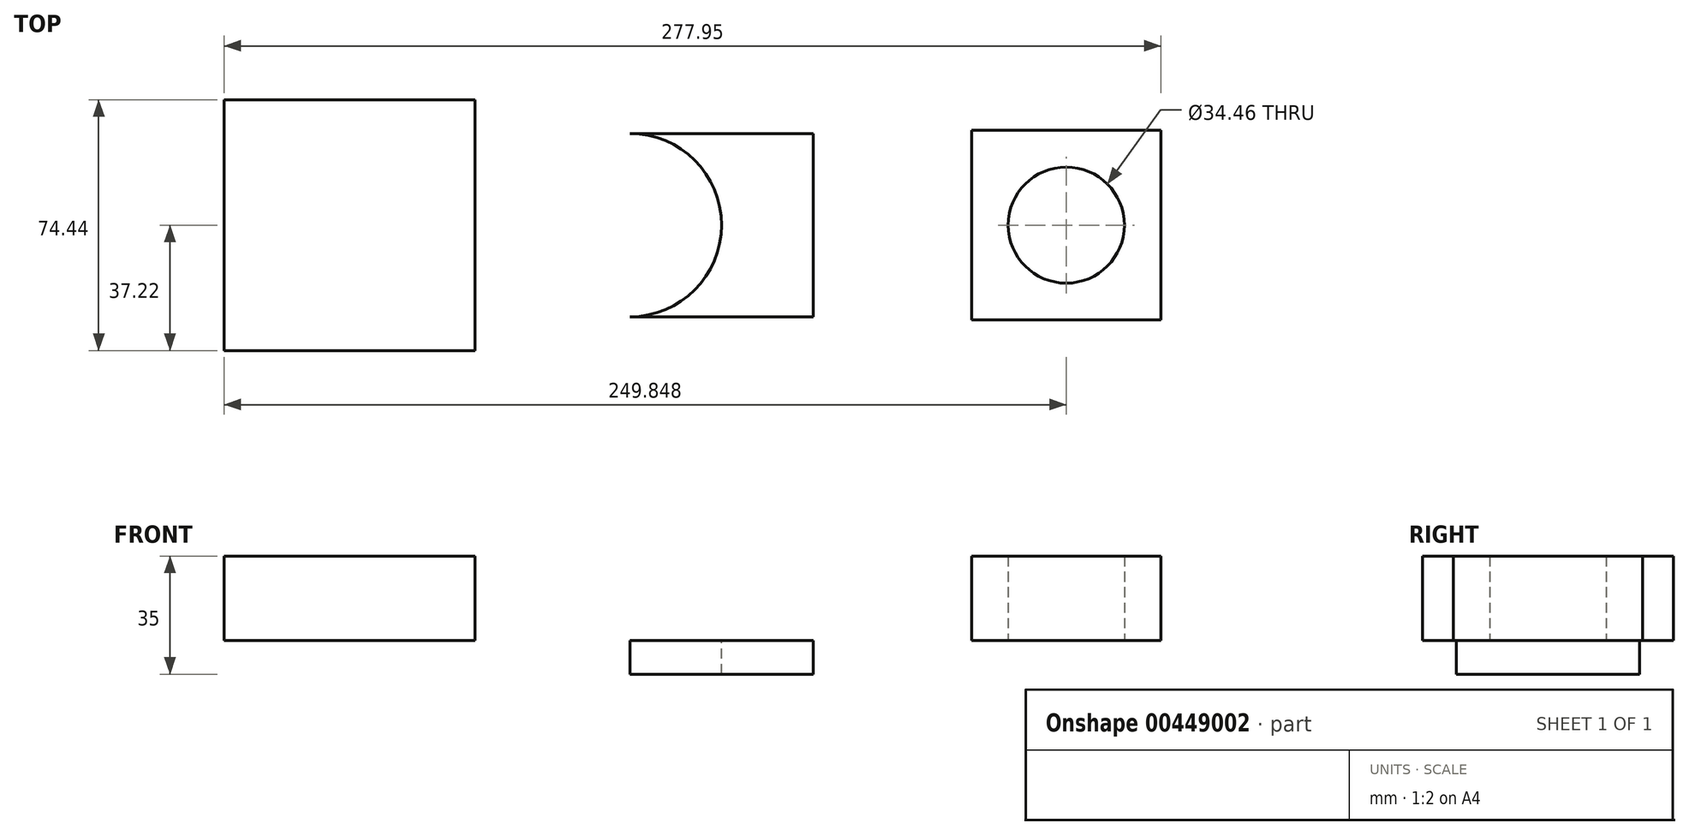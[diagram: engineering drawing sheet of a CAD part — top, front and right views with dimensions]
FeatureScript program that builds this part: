
annotation { "Feature Type Name" : "Feature", "Feature Type Description" : "" }
export const myFeature = defineFeature(function(context is Context, id is Id, definition is map)
    precondition{}
    {
        {
            var Q0;
            Q0=qCreatedBy(makeId("Top.planeOp"),FACE);
            var sketch = newSketch(context, id + "F0", { "sketchPlane" : qUnion([Q0])});
            skLineSegment(sketch, "E0.bottom", {"start": v(-37.22, 37.22) * mm, "end": v(37.22, 37.22) * mm});
            skLineSegment(sketch, "E0.top", {"start": v(-37.22, -37.22) * mm, "end": v(37.22, -37.22) * mm});
            skLineSegment(sketch, "E0.left", {"start": v(-37.22, 37.22) * mm, "end": v(-37.22, -37.22) * mm});
            skLineSegment(sketch, "E0.right", {"start": v(37.22, 37.22) * mm, "end": v(37.22, -37.22) * mm});
            skPoint(sketch, "E0.middle", {"position": v(0, 0) * mm});
            skSolve(sketch);
        }
        {
            var Q0;
            Q0=makeQuery(id+"F0.imprint","IMPRINT",FACE,{"disambiguationData":[TD([[makeQuery(id+"F0.imprint","IMPRINT",EDGE,{"derivedFrom":sQuery(id+"F0.wireOp",EDGE,"E0.bottom")}),-1.0]])]});
            extrude(context, id + "F1", {"entities" : qUnion([Q0]), "depth" : 25 * mm});
        }
        {
            var Q0;
            Q0=qCreatedBy(makeId("Top.planeOp"),FACE);
            var sketch = newSketch(context, id + "F2", { "sketchPlane" : qUnion([Q0])});
            skLineSegment(sketch, "E1.bottom", {"start": v(83.19, 27.19) * mm, "end": v(137.56, 27.19) * mm});
            skLineSegment(sketch, "E1.top", {"start": v(83.19, -27.19) * mm, "end": v(137.56, -27.19) * mm});
            skLineSegment(sketch, "E1.left", {"start": v(83.19, 27.19) * mm, "end": v(83.19, -27.19) * mm});
            skLineSegment(sketch, "E1.right", {"start": v(137.56, 27.19) * mm, "end": v(137.56, -27.19) * mm});
            skPoint(sketch, "E1.middle", {"position": v(110.37, 0) * mm});
            skArc(sketch, "E2", {"start": v(83.19, -27.19) * mm, "mid": v(110.37, 0) * mm, "end": v(83.19, 27.19) * mm});
            skSolve(sketch);
        }
        {
            var Q0;
            Q0=makeQuery(id+"F2.imprint","IMPRINT",FACE,{"disambiguationData":[TD([[makeQuery(id+"F2.imprint","IMPRINT",EDGE,{"derivedFrom":sQuery(id+"F2.wireOp",EDGE,"E1.bottom")}),-1.0]])]});
            extrude(context, id + "F3", {"entities" : qUnion([Q0]), "oppositeDirection" : true, "depth" : 10 * mm});
        }
        {
            var Q0;
            Q0=qCreatedBy(makeId("Top.planeOp"),FACE);
            var sketch = newSketch(context, id + "F4", { "sketchPlane" : qUnion([Q0])});
            skLineSegment(sketch, "E3.bottom", {"start": v(184.53, 28.1) * mm, "end": v(240.73, 28.1) * mm});
            skLineSegment(sketch, "E3.top", {"start": v(184.53, -28.1) * mm, "end": v(240.73, -28.1) * mm});
            skLineSegment(sketch, "E3.left", {"start": v(184.53, 28.1) * mm, "end": v(184.53, -28.1) * mm});
            skLineSegment(sketch, "E3.right", {"start": v(240.73, 28.1) * mm, "end": v(240.73, -28.1) * mm});
            skPoint(sketch, "E3.middle", {"position": v(212.63, 0) * mm});
            skCircle(sketch, "E4", {"center": v(212.63, 0) * mm, "radius": 17.23 * mm});
            skSolve(sketch);
        }
        {
            var Q0;
            Q0=qSketchRegion(id+"F4",true);
            extrude(context, id + "F5", {"entities" : qUnion([Q0]), "depth" : 25 * mm});
        }
    });
